# Revit family: Boiler-WeilMcLain-Aquabalance_Combination
name_source: partatom
category: Mechanical Equipment
revit_build: Autodesk Revit 2015 (Build: 20140606_1530(x64)
units: mm (PartAtom-declared; Revit-internal decimal feet)

## types (3) — shared parameters
Cold Water Supply = 1"
Combustion Air = 3"
Default Elevation = 4' - 0"
Depth = 1' - 0 19/32"
Description = Gas Boiler
Flue Outlet = 3"
Frequency = 60 Hz
Gas Connection = 1"
Heating System Return = 1"
Heating System Supply = 1"
Heating System Tapping = 3/8"
Height = 2' - 3 9/16"
Hot Water Outlet = 1"
Manufacturer = Weil-McLain
Number of Poles = 1
Phase = 1
Power Factor = 1
Product Documentation Link = http://aquabalanceboiler.com
Product Name = Aquabalance
Product Page URL = http://aquabalanceboiler.com
URL = https://www.weil-mclain.com
Voltage = 120 V
Width = 1' - 4 17/32"

## per-type parameters (varying)
| type | 3 | 4 | 5 | A | Actual Heating Water Flow | B | C | Domestic Hot Water | Model |
| WMB-80 | 2 7/32" | 2 7/32" | 3 3/8" | 4 1/8" | 2 GPM | 4 23/32" | 7 11/32" | 1" | WMB-80 Combination |
| WMB-120 | 2 7/32" | 2 7/32" | 3 3/8" | 4 1/8" | 3 GPM | 4 23/32" | 7 11/32" | 0" | WMB-120 Combination |
| WMB-155 | 3 5/8" | 2 1/16" | 2 13/32" | 6 3/32" | 4 GPM | 7 3/8" | 9 1/8" | 1" | WMB-155 Combination |

## geometry (parser evidence)
native form markers: Blend x11, Sweep x2
no freeform markers — native parametric forms only
